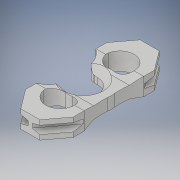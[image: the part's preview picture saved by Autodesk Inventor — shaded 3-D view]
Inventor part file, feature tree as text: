
AUTODESK INVENTOR PART (.ipt)
format: ipt  version: 2017 (Build 210142000, 142)  size: 622,592 bytes
history: native  units: in
note: dims shown in document units (in); Inventor stores cm internally (conversion verified against a paired STEP export)
features: projected_geometry x32, sketch x15, extrude x14, chamfer x8, fillet x2, revolve x1
ambient origin geometry x8: Origin, YZ Plane, XZ Plane, XY Plane, X Axis, Y Axis, Z Axis, Center Point
bodies: Body1 (feature_tree), Body2 (feature_tree)
feature tree (72):
  extrude  "Extrusion11"  Depth=0.1125in
  extrude  "Extrusion12"  Depth=0.0205in TaperAngle=0.0deg
  chamfer  "Chamfer17"  Distance=0.0627in Angle=45.0deg
  chamfer  "Chamfer18"  Distance=0.0627in Angle=45.0deg
  chamfer  "Chamfer19"  Distance=0.0627in Angle=45.0deg
  chamfer  "Chamfer20"  Distance=0.0627in Angle=45.0deg
  extrude  "Extrusion13"  Depth=0.0205in TaperAngle=0.0deg
  extrude  "Extrusion14"  Depth=0.0627in TaperAngle=45.0deg
  extrude  "Extrusion15"  Depth=0.0627in TaperAngle=45.0deg
  chamfer  "Chamfer21"  Distance=0.0627in Angle=45.0deg
  chamfer  "Chamfer22"  Distance=0.125in
  chamfer  "Chamfer23"  Distance=1.0in
  chamfer  "Chamfer24"  Distance=0.03in
  extrude  "Extrusion16"  Depth=0.03in
  fillet  "Fillet1"  [1 undecoded]
  extrude  "Extrusion17"  TaperAngle=90.0deg  [1 undecoded]
  fillet  "Fillet2"  Radius=0.03in
  extrude  "Extrusion18"  Depth=1.0in TaperAngle=0.0deg
  extrude  "Extrusion19"  Depth=1.0in TaperAngle=0.0deg
  extrude  "Extrusion22"  TaperAngle=90.0deg  [1 undecoded]
  extrude  "Extrusion25"  TaperAngle=120.0deg  [1 undecoded]
  extrude  "Extrusion26"  Depth=0.01in
  revolve  "Revolution1"  [1 undecoded]
  extrude  "Extrusion27"  Depth=0.185in TaperAngle=0.0deg
  extrude  "Extrusion28"  Depth=1.0in TaperAngle=0.0deg
  sketch  "Sketch1"  dims[d8=0.25in d83=0.1125in]
  sketch  "Sketch12"  dims[d84=0.02in d85=0.0in d86=0.0205in d87=0.0in d88=0.0627in d89=0.0205in d90=45.0deg d91=0.0627in d92=0.0205in d93=45.0deg d94=0.0627in d95=0.0205in d96=45.0deg d97=0.0627in d98=0.0205in d99=45.0deg]
  projected_geometry  "Projected Loop3"
  sketch  "Sketch14"  dims[d100=0.044in d101=0.0in d102=0.0205in d103=0.0in]
  projected_geometry  "Projected Loop4"
  sketch  "Sketch15"  dims[d104=0.02in d105=0.0in d106=0.0627in d107=0.0205in d108=45.0deg]
  projected_geometry  "Projected Loop5"
  projected_geometry  "Projected Loop6"
  sketch  "Sketch16"  dims[d109=0.0627in d110=0.0205in d111=45.0deg d112=0.0627in d113=0.0205in d114=45.0deg d115=0.0627in d116=0.0205in d117=45.0deg]
  projected_geometry  "Projected Loop7"
  sketch  "Sketch18"  dims[d119=0.45in d120=0.125in d121=0.0in]
  projected_geometry  "Projected Loop8"
  projected_geometry  "Projected Loop9"
  sketch  "Sketch19"  dims[d122=0.125in]
  projected_geometry  "Projected Loop10"
  projected_geometry  "Projected Loop11"
  projected_geometry  "Projected Loop12"
  projected_geometry  "Projected Loop13"
  sketch  "Sketch20"  dims[d123=0.3in]
  sketch  "Sketch21"  dims[d124=0.3in d125=1.0in d126=0.0in]
  sketch  "Sketch24"  dims[d127=0.1in d131=0.03in d132=0.0in]
  projected_geometry  "Projected Loop28"
  projected_geometry  "Projected Loop29"
  sketch  "Sketch29"  dims[d136=0.03in d137=0.0in d150=0.03in d151=90.0deg]
  sketch  "Sketch30"  dims[d152=0.03in d153=90.0deg d154=0.03in d155=0.0in]
  projected_geometry  "Projected Loop32"
  sketch  "Sketch31"  dims[d162=0.3in d169=1.0in d170=0.0in]
  projected_geometry  "Projected Loop33"
  projected_geometry  "Projected Loop36"
  sketch  "Sketch32"  dims[d175=0.04in d176=1.0in d177=0.0in]
  projected_geometry  "Projected Loop37"
  projected_geometry  "Projected Loop38"
  projected_geometry  "Projected Loop39"
  projected_geometry  "Projected Loop40"
  sketch  "Sketch33"  dims[d179=0.06in d180=90.0deg d181=120.0deg d182=0.01in d183=0.01in d184=0.185in d185=0.0in d186=1.0in d187=0.0in]
  projected_geometry  "Projected Loop41"
  projected_geometry  "Projected Loop42"
  projected_geometry  "Projected Loop43"
  projected_geometry  "Projected Loop44"
  projected_geometry  "Projected Loop45"
  projected_geometry  "Projected Loop46"
  projected_geometry  "Projected Loop47"
  projected_geometry  "Projected Loop48"
  projected_geometry  "Projected Loop49"
  projected_geometry  "Projected Loop50"
  projected_geometry  "Projected Loop51"
  projected_geometry  "Projected Loop52"
note: 5 required parameter values undecoded (feature->parameter linkage not recoverable at this tier; creation-order binding heuristic only, values carry confidence <= 0.55)